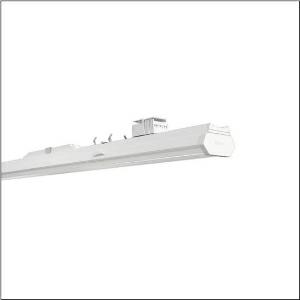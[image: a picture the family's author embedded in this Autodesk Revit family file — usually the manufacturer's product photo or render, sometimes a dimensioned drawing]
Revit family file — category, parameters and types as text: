
# Revit family: licross_r__21_protected_ho_52td1bmn4exm_7a17
name_source: partatom
category: Lighting Fixtures
units: mm (PartAtom-declared; Revit-internal decimal feet)

## family parameters
Cut with Voids When Loaded = No
Host = Face
Light Source = No
Part Type = Normal
Room Calculation Point = No
Round Connector Dimension = Use Diameter
Shared = No

## types (1)
- --- (1 x LED, 14040 lm, 83.2 W, 4000K)
    Apparent Load = 83 VA
    CIE Flux Codes = 54 82 95 97 100
    Color Rendering = 80
    Color Temperature = 4000K
    Default Elevation = 1800 mm
    Description = Licross® 21 Protected HO, luminaire insert, of sheet steel, galvanised, coil coated, white, length: 1.500mm, width: 90mm, height: 103mm, LED rated luminous flux: 14.040lm, light colour: 840, control gear: ON/OFF Multilumen, with plug, 3-pole, with phase selection, mains connection: 220..240V, AC, 50/60Hz, rated input power: 83W, internal wiring halogen-free, primary optical cover: cover, of PMMA, light emission: direct distribution, primary light characteristic: symmetric, protection rating (complete): IP54, insulation class (complete): insulation class I (protective earthing), certification: CE, ENEC, VDE, UKCA, protection symbol: D if used in an environment with non-conductive dust loads with corresponding accessories, impact resistance: IK06, permissible ambient temperature for indoor applications: -35..+35°C, corresponds to IFS (International Featured Standards) requirements for safety and quality in the food industry, reducing of maximum allowable ambient temperature of 5°C with ceiling mounting, LABS conformity tested according to VDMA 24364:2018-05, packaging unit: 1 piece
    Height = 92 mm
    Lamp = 1 x LED
    Lamp Light Flux = 14040 lm
    Lamp Power = 83.2 W
    Lamp count = 1
    Length = 1500 mm
    Luminous efficacy = 169 lm/W
    Manufacturer = Siteco
    ModVariant = No
    Model = 52TD1BMN4EXM
    Mounting Place = Ceiling
    Mounting Type = Pendant
    Number of Poles = 1
    OnlyDefault = Yes
    Power Factor = 1
    Product Name = Licross® 21 Protected HO
    Product group = luminaire insert | ceiling pendant
    ProductGroupID = 902
    Protection Class = Protection class I
    Protection Degree = IP 54
    RLX_Detail_Level = 1
    RLX_Emergency_Light_Flux = 0 lm
    RLX_Emergency_Type = 0
    RLX_Emergency_Type_DB = No
    RlxData = <blob elided: 22077 chars, md5=f9f5a025>
    Socket = socket
    Standby Power = 0 W
    System Light Flux = 14040 lm
    System Power = 83 W
    Type Comments = factory setting: luminous flux: 100 % | (A | C | E) | 195 mA
    Type Image = l_1256148.jpg
    URL = http://relux.com
    VarID = @adj_130641
    Voltage = 0 V
    Weight = 0.00 kg
    Width = 88 mm

## geometry (parser evidence)
native form markers: Blend x4, Sweep x11
no freeform markers — native parametric forms only
